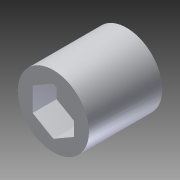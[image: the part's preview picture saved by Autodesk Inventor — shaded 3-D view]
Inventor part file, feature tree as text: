
AUTODESK INVENTOR PART (.ipt)
format: ipt  version: 2012 (Build 160160000, 160)  size: 135,680 bytes
history: native  units: in
note: dims shown in document units (in); Inventor stores cm internally (conversion verified against a paired STEP export)
features: sketch x6, extrude x6, plane x3, reference x1
ambient origin geometry x8: Origin, YZ Plane, XZ Plane, XY Plane, X Axis, Y Axis, Z Axis, Center Point
feature tree (16):
  sketch  "Sketch2"  dims[d5=0.3937in d6=0.0in d7=0.4724in d8=0.0in]
  plane  "Work Plane1"
  plane  "Work Plane2"
  plane  "Work Plane3"
  extrude  "Extrusion3"  Depth=0.4724in TaperAngle=0.0deg
  extrude  "Extrusion4"  Depth=0.0098in
  extrude  "Extrusion5"  Depth=0.0098in
  extrude  "Extrusion6"  Depth=0.0098in
  extrude  "Extrusion7"  Depth=0.0118in TaperAngle=0.0deg
  extrude  "Extrusion8"  Depth=0.1693in
  reference  "Reference1"
  sketch  "Sketch4"  dims[d9=0.0787in d10=0.0098in]
  sketch  "Sketch5"  dims[d11=0.0098in d12=0.0098in]
  sketch  "Sketch6"  dims[d13=0.0098in d14=0.0098in]
  sketch  "Sketch7"  dims[d15=0.0098in d16=0.0118in d17=0.0in]
  sketch  "Sketch10"  dims[d19=0.2756in d20=0.0in d21=0.1693in d22=0.2756in d23=0.0in d25=0.3543in d26=0.0394in d27=0.0in d32=0.0in d35=0.4764in]
